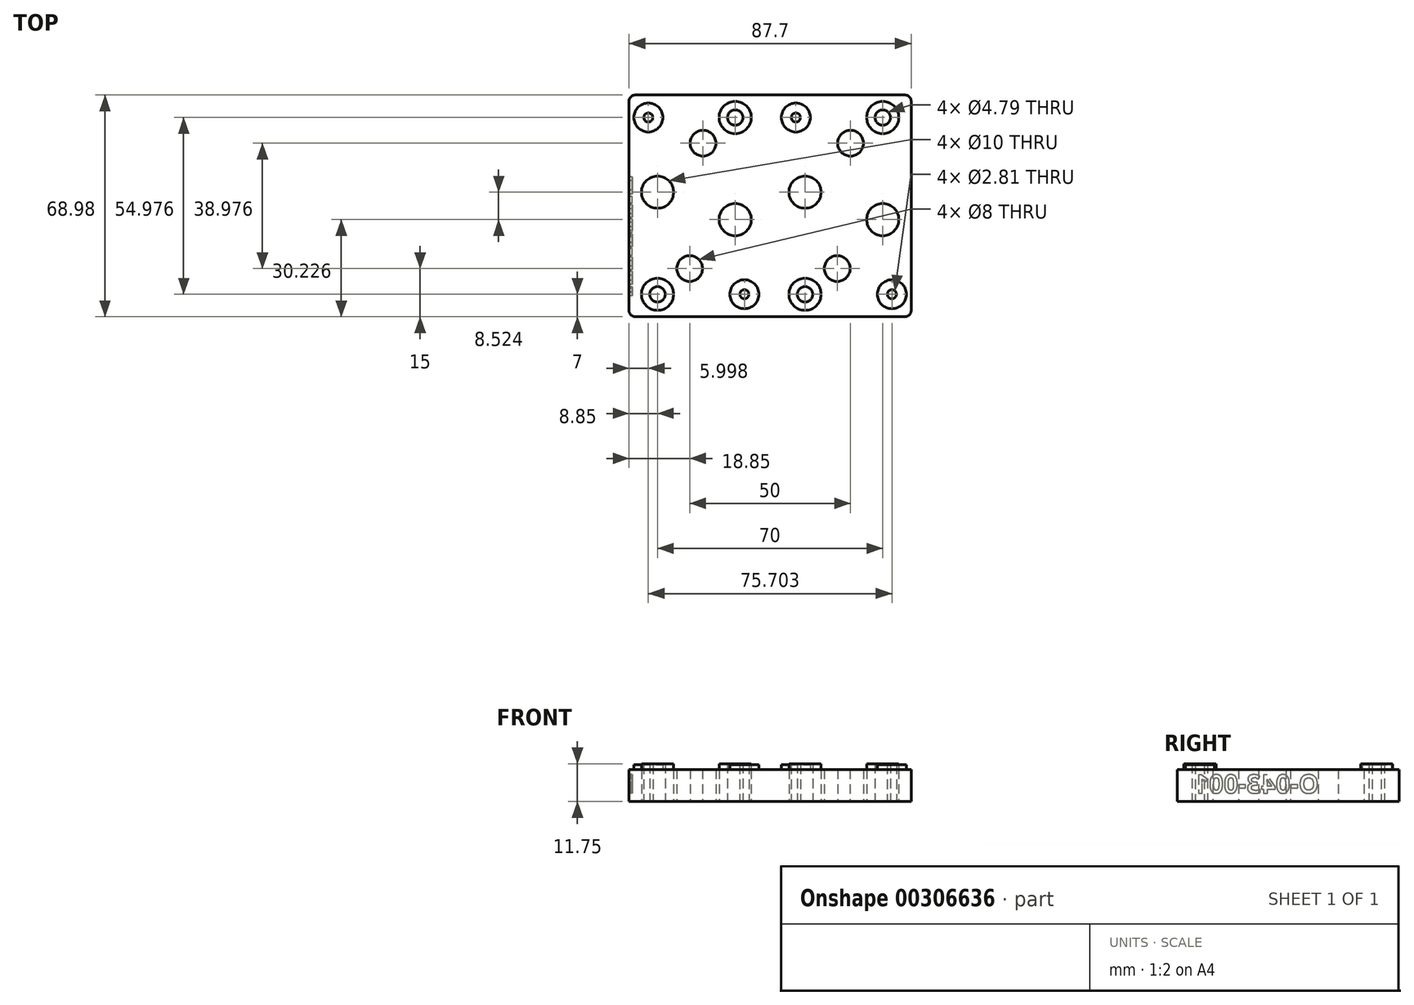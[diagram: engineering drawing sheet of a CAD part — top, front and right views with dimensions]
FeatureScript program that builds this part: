
annotation { "Feature Type Name" : "Feature", "Feature Type Description" : "" }
export const myFeature = defineFeature(function(context is Context, id is Id, definition is map)
    precondition{}
    {
        {
            var Q0;
            Q0=qCreatedBy(makeId("Top.planeOp"),FACE);
            var sketch = newSketch(context, id + "F0", { "sketchPlane" : qUnion([Q0])});
            skLineSegment(sketch, "E0.bottom", {"start": v(-43.85, 0) * mm, "end": v(43.85, 0) * mm});
            skLineSegment(sketch, "E0.top", {"start": v(-43.85, 68.98) * mm, "end": v(43.85, 68.98) * mm});
            skLineSegment(sketch, "E0.left", {"start": v(-43.85, 0) * mm, "end": v(-43.85, 68.98) * mm});
            skLineSegment(sketch, "E0.right", {"start": v(43.85, 0) * mm, "end": v(43.85, 68.98) * mm});
            skCircle(sketch, "E1", {"center": v(-37.85, 61.98) * mm, "radius": 1.4 * mm});
            skCircle(sketch, "E2", {"center": v(-35, 38.75) * mm, "radius": 5 * mm});
            skCircle(sketch, "E3", {"center": v(-25, 15) * mm, "radius": 4 * mm});
            skCircle(sketch, "E4", {"center": v(-35, 7) * mm, "radius": 2.4 * mm});
            skLineSegment(sketch, "E5", {"start": v(-35, 38.75) * mm, "end": v(-35, 7) * mm, "construction": true});
            skLineSegment(sketch, "E6", {"start": v(-37.85, 61.98) * mm, "end": v(-35, 38.75) * mm, "construction": true});
            skLineSegment(sketch, "E7", {"start": v(-37.85, 68.98) * mm, "end": v(-37.85, 0) * mm, "construction": true});
            skCircle(sketch, "E8", {"center": v(-35, 38.75) * mm, "radius": 7.5 * mm, "construction": true});
            skCircle(sketch, "E9", {"center": v(-8, 7) * mm, "radius": 1.4 * mm});
            skCircle(sketch, "E10", {"center": v(-10.85, 30.23) * mm, "radius": 5 * mm});
            skCircle(sketch, "E11", {"center": v(-20.85, 53.98) * mm, "radius": 4 * mm});
            skCircle(sketch, "E12", {"center": v(-10.85, 61.98) * mm, "radius": 2.4 * mm});
            skLineSegment(sketch, "E13", {"start": v(-10.85, 30.23) * mm, "end": v(-8, 7) * mm, "construction": true});
            skLineSegment(sketch, "E14", {"start": v(-8, 0) * mm, "end": v(-8, 37.05) * mm, "construction": true});
            skLineSegment(sketch, "E15", {"start": v(-10.85, 30.23) * mm, "end": v(-10.85, 61.98) * mm, "construction": true});
            skCircle(sketch, "E16", {"center": v(-10.85, 30.23) * mm, "radius": 7.5 * mm, "construction": true});
            skCircle(sketch, "E17", {"center": v(8, 61.98) * mm, "radius": 1.4 * mm});
            skCircle(sketch, "E18", {"center": v(10.85, 38.75) * mm, "radius": 5 * mm});
            skCircle(sketch, "E19", {"center": v(10.85, 7) * mm, "radius": 2.4 * mm});
            skCircle(sketch, "E20", {"center": v(20.85, 15) * mm, "radius": 4 * mm});
            skLineSegment(sketch, "E21", {"start": v(8, 61.98) * mm, "end": v(10.85, 38.75) * mm, "construction": true});
            skLineSegment(sketch, "E22", {"start": v(8, 61.98) * mm, "end": v(8, 33.09) * mm, "construction": true});
            skCircle(sketch, "E23", {"center": v(37.85, 7) * mm, "radius": 1.4 * mm});
            skCircle(sketch, "E24", {"center": v(35, 30.23) * mm, "radius": 5 * mm});
            skCircle(sketch, "E25", {"center": v(35, 61.98) * mm, "radius": 2.4 * mm});
            skCircle(sketch, "E26", {"center": v(25, 53.98) * mm, "radius": 4 * mm});
            skLineSegment(sketch, "E27", {"start": v(37.85, 7) * mm, "end": v(35, 30.23) * mm, "construction": true});
            skLineSegment(sketch, "E28", {"start": v(37.85, 0) * mm, "end": v(37.85, 32) * mm, "construction": true});
            skCircle(sketch, "E29", {"center": v(10.85, 38.75) * mm, "radius": 7.5 * mm, "construction": true});
            skCircle(sketch, "E30", {"center": v(35, 30.23) * mm, "radius": 7.5 * mm, "construction": true});
            skSolve(sketch);
        }
        {
            var Q0;
            Q0=makeQuery(id+"F0.imprint","IMPRINT",FACE,{"disambiguationData":[TD([[makeQuery(id+"F0.imprint","IMPRINT",EDGE,{"derivedFrom":sQuery(id+"F0.wireOp",EDGE,"E0.bottom")}),1.0]])]});
            extrude(context, id + "F1", {"entities" : qUnion([Q0]), "depth" : 10 * mm});
        }
        {
            var Q0;
            Q0=makeQuery(id+"F1.opExtrude","SWEPT_EDGE",EDGE,{"disambiguationData":[OSD([sQuery(id+"F0.wireOp",EDGE,"E0.bottom"),sQuery(id+"F0.wireOp",EDGE,"E0.left")])]});
            var Q1;
            Q1=makeQuery(id+"F1.opExtrude","SWEPT_EDGE",EDGE,{"disambiguationData":[OSD([sQuery(id+"F0.wireOp",EDGE,"E0.bottom"),sQuery(id+"F0.wireOp",EDGE,"E0.right")])]});
            var Q2;
            Q2=makeQuery(id+"F1.opExtrude","SWEPT_EDGE",EDGE,{"disambiguationData":[OSD([sQuery(id+"F0.wireOp",EDGE,"E0.top"),sQuery(id+"F0.wireOp",EDGE,"E0.right")])]});
            var Q3;
            Q3=makeQuery(id+"F1.opExtrude","SWEPT_EDGE",EDGE,{"disambiguationData":[OSD([sQuery(id+"F0.wireOp",EDGE,"E0.top"),sQuery(id+"F0.wireOp",EDGE,"E0.left")])]});
            var Q4;
            Q4=makeQuery(id+"Fm9VlG4bkvHOm0L_1.opExtrude","SWEPT_EDGE",EDGE,{"disambiguationData":[OSD([sQuery(id+"F0.wireOp",EDGE,"QbjodZTt-SxHU-iwYF-6VFG-K2zBgEWIyztY.top"),sQuery(id+"F0.wireOp",EDGE,"QbjodZTt-SxHU-iwYF-6VFG-K2zBgEWIyztY.left")])]});
            var Q5;
            Q5=makeQuery(id+"Fm9VlG4bkvHOm0L_1.opExtrude","SWEPT_EDGE",EDGE,{"disambiguationData":[OSD([sQuery(id+"F0.wireOp",EDGE,"QbjodZTt-SxHU-iwYF-6VFG-K2zBgEWIyztY.bottom"),sQuery(id+"F0.wireOp",EDGE,"QbjodZTt-SxHU-iwYF-6VFG-K2zBgEWIyztY.left")])]});
            var Q6;
            Q6=makeQuery(id+"Fm9VlG4bkvHOm0L_1.opExtrude","SWEPT_EDGE",EDGE,{"disambiguationData":[OSD([sQuery(id+"F0.wireOp",EDGE,"QbjodZTt-SxHU-iwYF-6VFG-K2zBgEWIyztY.top"),sQuery(id+"F0.wireOp",EDGE,"QbjodZTt-SxHU-iwYF-6VFG-K2zBgEWIyztY.right")])]});
            var Q7;
            Q7=makeQuery(id+"Fm9VlG4bkvHOm0L_1.opExtrude","SWEPT_EDGE",EDGE,{"disambiguationData":[OSD([sQuery(id+"F0.wireOp",EDGE,"QbjodZTt-SxHU-iwYF-6VFG-K2zBgEWIyztY.bottom"),sQuery(id+"F0.wireOp",EDGE,"QbjodZTt-SxHU-iwYF-6VFG-K2zBgEWIyztY.right")])]});
            fillet(context, id + "F2", {"entities" : qUnion([Q0, Q1, Q2, Q3, Q4, Q5, Q6, Q7]), "radius" : 2 * mm, "tangentPropagation" : true, "allowEdgeOverflow" : false});
        }
        {
            var Q0;
            Q0=makeQuery(id+"F1.opExtrude","CAP_FACE",FACE,{"disambiguationData":[OSD([sQuery(id+"F0.wireOp",EDGE,"E0.bottom"),sQuery(id+"F0.wireOp",EDGE,"E0.top"),sQuery(id+"F0.wireOp",EDGE,"E0.left"),sQuery(id+"F0.wireOp",EDGE,"E0.right"),sQuery(id+"F0.wireOp",EDGE,"E1"),sQuery(id+"F0.wireOp",EDGE,"E2"),sQuery(id+"F0.wireOp",EDGE,"E3"),sQuery(id+"F0.wireOp",EDGE,"E4"),sQuery(id+"F0.wireOp",EDGE,"E9"),sQuery(id+"F0.wireOp",EDGE,"E10"),sQuery(id+"F0.wireOp",EDGE,"E11"),sQuery(id+"F0.wireOp",EDGE,"E12"),sQuery(id+"F0.wireOp",EDGE,"E17"),sQuery(id+"F0.wireOp",EDGE,"E18"),sQuery(id+"F0.wireOp",EDGE,"E19"),sQuery(id+"F0.wireOp",EDGE,"E20"),sQuery(id+"F0.wireOp",EDGE,"E23"),sQuery(id+"F0.wireOp",EDGE,"E24"),sQuery(id+"F0.wireOp",EDGE,"E25"),sQuery(id+"F0.wireOp",EDGE,"E26")])],"isStart":false});
            var sketch = newSketch(context, id + "F3", { "sketchPlane" : qUnion([Q0])});
            skCircle(sketch, "E31", {"center": v(-37.85, 61.98) * mm, "radius": 4.5 * mm});
            skCircle(sketch, "E32", {"center": v(8, 61.98) * mm, "radius": 4.5 * mm});
            skCircle(sketch, "E33", {"center": v(35, 61.98) * mm, "radius": 5 * mm});
            skCircle(sketch, "E34", {"center": v(-35, 7) * mm, "radius": 5 * mm});
            skCircle(sketch, "E35", {"center": v(-8, 7) * mm, "radius": 4.5 * mm});
            skCircle(sketch, "E36", {"center": v(10.85, 7) * mm, "radius": 5 * mm});
            skCircle(sketch, "E37", {"center": v(37.85, 7) * mm, "radius": 4.5 * mm});
            skCircle(sketch, "E38", {"center": v(-10.85, 61.98) * mm, "radius": 5 * mm});
            skSolve(sketch);
        }
        {
            var Q0;
            Q0=makeQuery(id+"F3.imprint","IMPRINT",FACE,{"disambiguationData":[TD([[makeQuery(id+"F3.imprint","IMPRINT",EDGE,{"derivedFrom":sQuery(id+"F3.wireOp",EDGE,"E31")}),1.0]])]});
            var Q1;
            Q1=makeQuery(id+"F3.imprint","IMPRINT",FACE,{"disambiguationData":[TD([[makeQuery(id+"F3.imprint","IMPRINT",EDGE,{"derivedFrom":sQuery(id+"F3.wireOp",EDGE,"E32")}),1.0]])]});
            var Q2;
            Q2=makeQuery(id+"F3.imprint","IMPRINT",FACE,{"disambiguationData":[TD([[makeQuery(id+"F3.imprint","IMPRINT",EDGE,{"derivedFrom":sQuery(id+"F3.wireOp",EDGE,"E37")}),1.0]])]});
            var Q3;
            Q3=makeQuery(id+"F3.imprint","IMPRINT",FACE,{"disambiguationData":[TD([[makeQuery(id+"F3.imprint","IMPRINT",EDGE,{"derivedFrom":sQuery(id+"F3.wireOp",EDGE,"E35")}),1.0]])]});
            extrude(context, id + "F4", {"entities" : qUnion([Q0, Q1, Q2, Q3]), "operationType" : NewBodyOperationType.ADD, "depth" : 1.5 * mm});
        }
        {
            var Q0;
            Q0=makeQuery(id+"F1.opExtrude","SWEPT_FACE",FACE,{"disambiguationData":[OSD([sQuery(id+"F0.wireOp",EDGE,"E0.left")])]});
            var sketch = newSketch(context, id + "F5", { "sketchPlane" : qUnion([Q0])});
            skText(sketch, "E39", { "text": "O-043-001", "fontName": "OpenSans-Bold.ttf"});
            skLineSegment(sketch, "E40", {"start": v(-2, 5.5) * mm, "end": v(-51.7, 5.5) * mm, "construction": true});
            skPoint(sketch, "E41", {"position": v(-25, 5.5) * mm});
            const initialGuessF5  = {"E39": [-0.044, 0.00263, 1, 0, 0.00573]};
            skSetInitialGuess(sketch, initialGuessF5);
            skSolve(sketch);
        }
        {
            var Q0;
            Q0=qSketchRegion(id+"F5",true);
            extrude(context, id + "F6", {"entities" : qUnion([Q0]), "operationType" : NewBodyOperationType.REMOVE, "oppositeDirection" : true, "depth" : 1 * mm});
        }
        {
            var Q0;
            Q0=makeQuery(id+"F3.imprint","IMPRINT",FACE,{"disambiguationData":[TD([[makeQuery(id+"F3.imprint","IMPRINT",EDGE,{"derivedFrom":sQuery(id+"F3.wireOp",EDGE,"E38")}),1.0]])]});
            var Q1;
            Q1=makeQuery(id+"F3.imprint","IMPRINT",FACE,{"disambiguationData":[TD([[makeQuery(id+"F3.imprint","IMPRINT",EDGE,{"derivedFrom":sQuery(id+"F3.wireOp",EDGE,"E34")}),1.0]])]});
            var Q2;
            Q2=makeQuery(id+"F3.imprint","IMPRINT",FACE,{"disambiguationData":[TD([[makeQuery(id+"F3.imprint","IMPRINT",EDGE,{"derivedFrom":sQuery(id+"F3.wireOp",EDGE,"E33")}),1.0]])]});
            var Q3;
            Q3=makeQuery(id+"F3.imprint","IMPRINT",FACE,{"disambiguationData":[TD([[makeQuery(id+"F3.imprint","IMPRINT",EDGE,{"derivedFrom":sQuery(id+"F3.wireOp",EDGE,"E36")}),1.0]])]});
            extrude(context, id + "F7", {"entities" : qUnion([Q0, Q1, Q2, Q3]), "operationType" : NewBodyOperationType.ADD, "depth" : 1.75 * mm});
        }
    });
